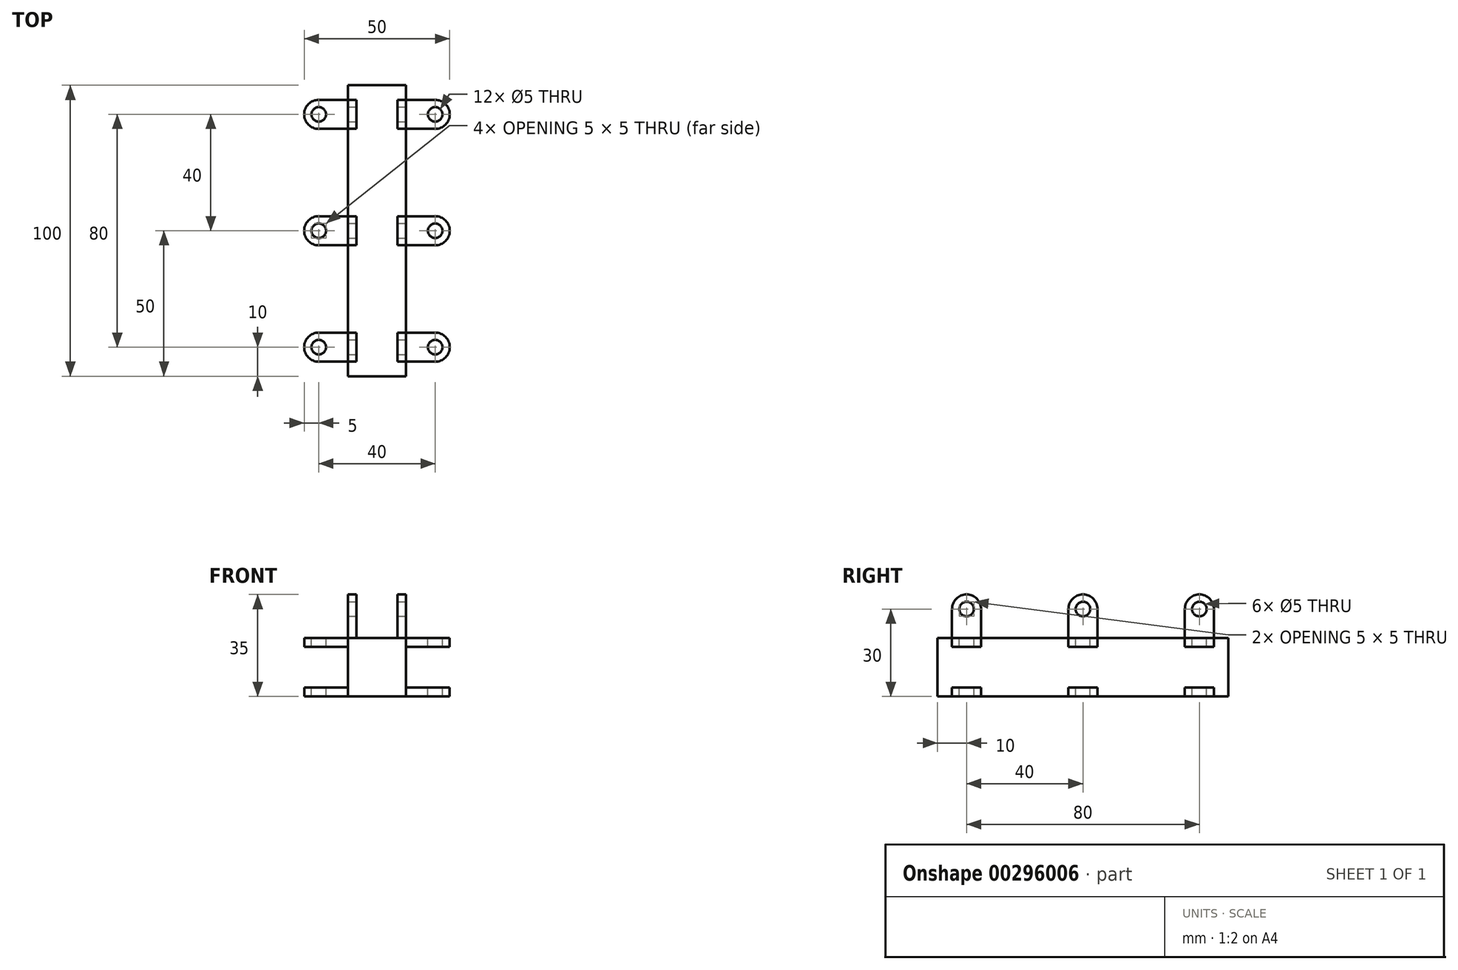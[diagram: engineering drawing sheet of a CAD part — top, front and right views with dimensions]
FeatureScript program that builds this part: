
annotation { "Feature Type Name" : "Feature", "Feature Type Description" : "" }
export const myFeature = defineFeature(function(context is Context, id is Id, definition is map)
    precondition{}
    {
        {
            var Q0;
            Q0=qCreatedBy(makeId("Front.planeOp"),FACE);
            var sketch = newSketch(context, id + "F0", { "sketchPlane" : qUnion([Q0])});
            skLineSegment(sketch, "E0.bottom", {"start": v(10, -10) * mm, "end": v(-10, -10) * mm});
            skLineSegment(sketch, "E0.top", {"start": v(10, 10) * mm, "end": v(-10, 10) * mm});
            skLineSegment(sketch, "E0.left", {"start": v(10, -10) * mm, "end": v(10, 10) * mm});
            skLineSegment(sketch, "E0.right", {"start": v(-10, -10) * mm, "end": v(-10, 10) * mm});
            skPoint(sketch, "E0.middle", {"position": v(0, 0) * mm});
            skSolve(sketch);
        }
        {
            var Q0;
            Q0=makeQuery(id+"F0.imprint","IMPRINT",FACE,{"disambiguationData":[TD([[makeQuery(id+"F0.imprint","IMPRINT",EDGE,{"derivedFrom":sQuery(id+"F0.wireOp",EDGE,"E0.bottom")}),-1.0]])]});
            extrude(context, id + "F1", {"entities" : qUnion([Q0]), "endBound" : BoundingType.SYMMETRIC, "depth" : 100 * mm});
        }
        {
            var Q0;
            Q0=qCreatedBy(makeId("Right.planeOp"),FACE);
            var sketch = newSketch(context, id + "F2", { "sketchPlane" : qUnion([Q0])});
            skLineSegment(sketch, "E1.bottom", {"start": v(-45, 10) * mm, "end": v(-35, 10) * mm});
            skLineSegment(sketch, "E1.top", {"start": v(-45, 7) * mm, "end": v(-35, 7) * mm});
            skLineSegment(sketch, "E1.left", {"start": v(-45, 10) * mm, "end": v(-45, 7) * mm});
            skLineSegment(sketch, "E1.right", {"start": v(-35, 10) * mm, "end": v(-35, 7) * mm});
            skLineSegment(sketch, "E2.MirrorCS", {"start": v(-35, -10) * mm, "end": v(-35, -7) * mm});
            skLineSegment(sketch, "E3.MirrorCS", {"start": v(-45, -10) * mm, "end": v(-45, -7) * mm});
            skLineSegment(sketch, "E4.MirrorCS", {"start": v(-45, -7) * mm, "end": v(-35, -7) * mm});
            skLineSegment(sketch, "E5.MirrorCS", {"start": v(-45, -10) * mm, "end": v(-35, -10) * mm});
            skLineSegment(sketch, "E6.MirrorCS", {"start": v(45, -10) * mm, "end": v(45, -7) * mm});
            skLineSegment(sketch, "E7.MirrorCS", {"start": v(35, -10) * mm, "end": v(35, -7) * mm});
            skLineSegment(sketch, "E8.MirrorCS", {"start": v(35, 10) * mm, "end": v(35, 7) * mm});
            skLineSegment(sketch, "E9.MirrorCS", {"start": v(45, 10) * mm, "end": v(45, 7) * mm});
            skLineSegment(sketch, "E10.MirrorCS", {"start": v(45, -7) * mm, "end": v(35, -7) * mm});
            skLineSegment(sketch, "E11.MirrorCS", {"start": v(45, 10) * mm, "end": v(35, 10) * mm});
            skLineSegment(sketch, "E12.MirrorCS", {"start": v(45, -10) * mm, "end": v(35, -10) * mm});
            skLineSegment(sketch, "E13.MirrorCS", {"start": v(45, 7) * mm, "end": v(35, 7) * mm});
            skLineSegment(sketch, "E14.bottom", {"start": v(5, 7) * mm, "end": v(-5, 7) * mm});
            skLineSegment(sketch, "E14.top", {"start": v(5, 10) * mm, "end": v(-5, 10) * mm});
            skLineSegment(sketch, "E14.left", {"start": v(5, 7) * mm, "end": v(5, 10) * mm});
            skLineSegment(sketch, "E14.right", {"start": v(-5, 7) * mm, "end": v(-5, 10) * mm});
            skPoint(sketch, "E14.middle", {"position": v(0, 8.5) * mm});
            skLineSegment(sketch, "E15.MirrorCS", {"start": v(5, -7) * mm, "end": v(5, -10) * mm});
            skLineSegment(sketch, "E16.MirrorCS", {"start": v(-5, -7) * mm, "end": v(-5, -10) * mm});
            skLineSegment(sketch, "E17.MirrorCS", {"start": v(5, -10) * mm, "end": v(-5, -10) * mm});
            skLineSegment(sketch, "E18.MirrorCS", {"start": v(5, -7) * mm, "end": v(-5, -7) * mm});
            skPoint(sketch, "E19.MirrorP", {"position": v(0, -8.5) * mm});
            skSolve(sketch);
        }
        {
            var Q0;
            Q0 = qSketchRegion(id + "F2", true);
            var Q1;
            Q1=makeQuery(id+"F1.opExtrude","SWEPT_FACE",FACE,{"disambiguationData":[OSD([sQuery(id+"F0.wireOp",EDGE,"E0.left")])]});
            extrude(context, id + "F3", {"entities" : qUnion([Q0]), "operationType" : NewBodyOperationType.ADD, "endBoundEntityFace" : qUnion([Q1]), "depth" : 25 * mm, "hasSecondDirection" : true, "secondDirectionOppositeDirection" : true, "secondDirectionDepth" : 25 * mm});
        }
        {
            var Q0;
            Q0=makeQuery(id+"F3.opExtrude","CAP_EDGE",EDGE,{"disambiguationData":[OSD([sQuery(id+"F2.wireOp",EDGE,"E1.left")])],"isStart":false});
            var Q1;
            Q1=makeQuery(id+"F3.opExtrude","CAP_EDGE",EDGE,{"disambiguationData":[OSD([sQuery(id+"F2.wireOp",EDGE,"E1.right")])],"isStart":false});
            var Q2;
            Q2=makeQuery(id+"F3.opExtrude","CAP_EDGE",EDGE,{"disambiguationData":[OSD([sQuery(id+"F2.wireOp",EDGE,"E3.MirrorCS")])],"isStart":false});
            var Q3;
            Q3=makeQuery(id+"F3.opExtrude","CAP_EDGE",EDGE,{"disambiguationData":[OSD([sQuery(id+"F2.wireOp",EDGE,"E2.MirrorCS")])],"isStart":false});
            var Q4;
            Q4=makeQuery(id+"F3.opExtrude","CAP_EDGE",EDGE,{"disambiguationData":[OSD([sQuery(id+"F2.wireOp",EDGE,"E14.right")])],"isStart":false});
            var Q5;
            Q5=makeQuery(id+"F3.opExtrude","CAP_EDGE",EDGE,{"disambiguationData":[OSD([sQuery(id+"F2.wireOp",EDGE,"E14.left")])],"isStart":false});
            var Q6;
            Q6=makeQuery(id+"F3.opExtrude","CAP_EDGE",EDGE,{"disambiguationData":[OSD([sQuery(id+"F2.wireOp",EDGE,"E16.MirrorCS")])],"isStart":false});
            var Q7;
            Q7=makeQuery(id+"F3.opExtrude","CAP_EDGE",EDGE,{"disambiguationData":[OSD([sQuery(id+"F2.wireOp",EDGE,"E15.MirrorCS")])],"isStart":false});
            var Q8;
            Q8=makeQuery(id+"F3.opExtrude","CAP_EDGE",EDGE,{"disambiguationData":[OSD([sQuery(id+"F2.wireOp",EDGE,"E8.MirrorCS")])],"isStart":false});
            var Q9;
            Q9=makeQuery(id+"F3.opExtrude","CAP_EDGE",EDGE,{"disambiguationData":[OSD([sQuery(id+"F2.wireOp",EDGE,"E9.MirrorCS")])],"isStart":false});
            var Q10;
            Q10=makeQuery(id+"F3.opExtrude","CAP_EDGE",EDGE,{"disambiguationData":[OSD([sQuery(id+"F2.wireOp",EDGE,"E7.MirrorCS")])],"isStart":false});
            var Q11;
            Q11=makeQuery(id+"F3.opExtrude","CAP_EDGE",EDGE,{"disambiguationData":[OSD([sQuery(id+"F2.wireOp",EDGE,"E6.MirrorCS")])],"isStart":false});
            fillet(context, id + "F4", {"entities" : qUnion([Q0, Q1, Q2, Q3, Q4, Q5, Q6, Q7, Q8, Q9, Q10, Q11]), "radius" : 5 * mm, "tangentPropagation" : true, "allowEdgeOverflow" : false});
        }
        {
            var Q0;
            Q0=qCreatedBy(makeId("Top.planeOp"),FACE);
            var sketch = newSketch(context, id + "F5", { "sketchPlane" : qUnion([Q0])});
            skCircle(sketch, "E20", {"center": v(20, -40) * mm, "radius": 2.5 * mm});
            skCircle(sketch, "E21.MirrorC", {"center": v(20, 40) * mm, "radius": 2.5 * mm});
            skCircle(sketch, "E22", {"center": v(20, 0) * mm, "radius": 2.5 * mm});
            skCircle(sketch, "E23.MirrorC", {"center": v(-20, -40) * mm, "radius": 2.5 * mm});
            skCircle(sketch, "E24.MirrorC", {"center": v(-20, 0) * mm, "radius": 2.5 * mm});
            skCircle(sketch, "E25.MirrorC", {"center": v(-20, 40) * mm, "radius": 2.5 * mm});
            skSolve(sketch);
        }
        {
            var Q0;
            Q0 = qSketchRegion(id + "F5", true);
            extrude(context, id + "F6", {"entities" : qUnion([Q0]), "operationType" : NewBodyOperationType.REMOVE, "endBound" : BoundingType.SYMMETRIC, "oppositeDirection" : true, "depth" : 20 * mm});
        }
        {
            var Q0;
            Q0=makeQuery(id+"F3.opExtrude","CAP_EDGE",EDGE,{"disambiguationData":[OSD([sQuery(id+"F2.wireOp",EDGE,"E3.MirrorCS")])],"isStart":true});
            var Q1;
            Q1=makeQuery(id+"F3.opExtrude","CAP_EDGE",EDGE,{"disambiguationData":[OSD([sQuery(id+"F2.wireOp",EDGE,"E2.MirrorCS")])],"isStart":true});
            var Q2;
            Q2=makeQuery(id+"F3.opExtrude","CAP_EDGE",EDGE,{"disambiguationData":[OSD([sQuery(id+"F2.wireOp",EDGE,"E1.left")])],"isStart":true});
            var Q3;
            Q3=makeQuery(id+"F3.opExtrude","CAP_EDGE",EDGE,{"disambiguationData":[OSD([sQuery(id+"F2.wireOp",EDGE,"E1.right")])],"isStart":true});
            var Q4;
            Q4=makeQuery(id+"F3.opExtrude","CAP_EDGE",EDGE,{"disambiguationData":[OSD([sQuery(id+"F2.wireOp",EDGE,"E16.MirrorCS")])],"isStart":true});
            var Q5;
            Q5=makeQuery(id+"F3.opExtrude","CAP_EDGE",EDGE,{"disambiguationData":[OSD([sQuery(id+"F2.wireOp",EDGE,"E15.MirrorCS")])],"isStart":true});
            var Q6;
            Q6=makeQuery(id+"F3.opExtrude","CAP_EDGE",EDGE,{"disambiguationData":[OSD([sQuery(id+"F2.wireOp",EDGE,"E14.right")])],"isStart":true});
            var Q7;
            Q7=makeQuery(id+"F3.opExtrude","CAP_EDGE",EDGE,{"disambiguationData":[OSD([sQuery(id+"F2.wireOp",EDGE,"E14.left")])],"isStart":true});
            var Q8;
            Q8=makeQuery(id+"F3.opExtrude","CAP_EDGE",EDGE,{"disambiguationData":[OSD([sQuery(id+"F2.wireOp",EDGE,"E7.MirrorCS")])],"isStart":true});
            var Q9;
            Q9=makeQuery(id+"F3.opExtrude","CAP_EDGE",EDGE,{"disambiguationData":[OSD([sQuery(id+"F2.wireOp",EDGE,"E6.MirrorCS")])],"isStart":true});
            var Q10;
            Q10=makeQuery(id+"F3.opExtrude","CAP_EDGE",EDGE,{"disambiguationData":[OSD([sQuery(id+"F2.wireOp",EDGE,"E8.MirrorCS")])],"isStart":true});
            var Q11;
            Q11=makeQuery(id+"F3.opExtrude","CAP_EDGE",EDGE,{"disambiguationData":[OSD([sQuery(id+"F2.wireOp",EDGE,"E9.MirrorCS")])],"isStart":true});
            fillet(context, id + "F7", {"entities" : qUnion([Q0, Q1, Q2, Q3, Q4, Q5, Q6, Q7, Q8, Q9, Q10, Q11]), "radius" : 5 * mm, "tangentPropagation" : true, "allowEdgeOverflow" : false});
        }
        {
            var Q0;
            Q0=qCreatedBy(makeId("Top.planeOp"),FACE);
            var sketch = newSketch(context, id + "F8", { "sketchPlane" : qUnion([Q0])});
            skLineSegment(sketch, "E26.bottom", {"start": v(10, -5) * mm, "end": v(7, -5) * mm});
            skLineSegment(sketch, "E26.top", {"start": v(10, 5) * mm, "end": v(7, 5) * mm});
            skLineSegment(sketch, "E26.left", {"start": v(10, -5) * mm, "end": v(10, 5) * mm});
            skLineSegment(sketch, "E26.right", {"start": v(7, -5) * mm, "end": v(7, 5) * mm});
            skLineSegment(sketch, "E27.MirrorCS", {"start": v(-7, -5) * mm, "end": v(-7, 5) * mm});
            skLineSegment(sketch, "E28.MirrorCS", {"start": v(-10, -5) * mm, "end": v(-10, 5) * mm});
            skLineSegment(sketch, "E29.MirrorCS", {"start": v(-10, 5) * mm, "end": v(-7, 5) * mm});
            skLineSegment(sketch, "E30.MirrorCS", {"start": v(-10, -5) * mm, "end": v(-7, -5) * mm});
            skLineSegment(sketch, "E31.bottom", {"start": v(10, 45) * mm, "end": v(7, 45) * mm});
            skLineSegment(sketch, "E31.top", {"start": v(10, 35) * mm, "end": v(7, 35) * mm});
            skLineSegment(sketch, "E31.left", {"start": v(10, 45) * mm, "end": v(10, 35) * mm});
            skLineSegment(sketch, "E31.right", {"start": v(7, 45) * mm, "end": v(7, 35) * mm});
            skLineSegment(sketch, "E32.MirrorCS", {"start": v(-7, 45) * mm, "end": v(-7, 35) * mm});
            skLineSegment(sketch, "E33.MirrorCS", {"start": v(-10, 45) * mm, "end": v(-10, 35) * mm});
            skLineSegment(sketch, "E34.MirrorCS", {"start": v(-10, 35) * mm, "end": v(-7, 35) * mm});
            skLineSegment(sketch, "E35.MirrorCS", {"start": v(-10, 45) * mm, "end": v(-7, 45) * mm});
            skLineSegment(sketch, "E36.MirrorCS", {"start": v(-7, -45) * mm, "end": v(-7, -35) * mm});
            skLineSegment(sketch, "E37.MirrorCS", {"start": v(7, -45) * mm, "end": v(7, -35) * mm});
            skLineSegment(sketch, "E38.MirrorCS", {"start": v(-10, -35) * mm, "end": v(-7, -35) * mm});
            skLineSegment(sketch, "E39.MirrorCS", {"start": v(-10, -45) * mm, "end": v(-7, -45) * mm});
            skLineSegment(sketch, "E40.MirrorCS", {"start": v(10, -45) * mm, "end": v(7, -45) * mm});
            skLineSegment(sketch, "E41.MirrorCS", {"start": v(10, -35) * mm, "end": v(7, -35) * mm});
            skLineSegment(sketch, "E42.MirrorCS", {"start": v(-10, -45) * mm, "end": v(-10, -35) * mm});
            skLineSegment(sketch, "E43.MirrorCS", {"start": v(10, -45) * mm, "end": v(10, -35) * mm});
            skSolve(sketch);
        }
        {
            var Q0;
            Q0 = qSketchRegion(id + "F8", true);
            extrude(context, id + "F9", {"entities" : qUnion([Q0]), "operationType" : NewBodyOperationType.ADD, "depth" : 25 * mm});
        }
        {
            var Q0;
            Q0=makeQuery(id+"F9.opExtrude","CAP_EDGE",EDGE,{"disambiguationData":[OSD([sQuery(id+"F8.wireOp",EDGE,"e20e8f79-4628-48e8-b713-7d486e24c0815.MirrorCS")])],"isStart":false});
            var Q1;
            Q1=makeQuery(id+"F9.opExtrude","CAP_EDGE",EDGE,{"disambiguationData":[OSD([sQuery(id+"F8.wireOp",EDGE,"e20e8f79-4628-48e8-b713-7d486e24c0817.MirrorCS")])],"isStart":false});
            var Q2;
            Q2=makeQuery(id+"F9.opExtrude","CAP_EDGE",EDGE,{"disambiguationData":[OSD([sQuery(id+"F8.wireOp",EDGE,"e20e8f79-4628-48e8-b713-7d486e24c0811.MirrorCS")])],"isStart":false});
            var Q3;
            Q3=makeQuery(id+"F9.opExtrude","CAP_EDGE",EDGE,{"disambiguationData":[OSD([sQuery(id+"F8.wireOp",EDGE,"e20e8f79-4628-48e8-b713-7d486e24c0812.MirrorCS")])],"isStart":false});
            var Q4;
            Q4=makeQuery(id+"F9.opExtrude","CAP_EDGE",EDGE,{"disambiguationData":[OSD([sQuery(id+"F8.wireOp",EDGE,"E26.bottom")])],"isStart":false});
            var Q5;
            Q5=makeQuery(id+"F9.opExtrude","CAP_EDGE",EDGE,{"disambiguationData":[OSD([sQuery(id+"F8.wireOp",EDGE,"E26.top")])],"isStart":false});
            var Q6;
            Q6=makeQuery(id+"F9.opExtrude","CAP_EDGE",EDGE,{"disambiguationData":[OSD([sQuery(id+"F8.wireOp",EDGE,"E30.MirrorCS")])],"isStart":false});
            var Q7;
            Q7=makeQuery(id+"F9.opExtrude","CAP_EDGE",EDGE,{"disambiguationData":[OSD([sQuery(id+"F8.wireOp",EDGE,"E29.MirrorCS")])],"isStart":false});
            var Q8;
            Q8=makeQuery(id+"F9.opExtrude","CAP_EDGE",EDGE,{"disambiguationData":[OSD([sQuery(id+"F8.wireOp",EDGE,"037edfc9-c22c-4f75-90ba-cc2340fa92b612.MirrorCS")])],"isStart":false});
            var Q9;
            Q9=makeQuery(id+"F9.opExtrude","CAP_EDGE",EDGE,{"disambiguationData":[OSD([sQuery(id+"F8.wireOp",EDGE,"037edfc9-c22c-4f75-90ba-cc2340fa92b611.MirrorCS")])],"isStart":false});
            var Q10;
            Q10=makeQuery(id+"F9.opExtrude","CAP_EDGE",EDGE,{"disambiguationData":[OSD([sQuery(id+"F8.wireOp",EDGE,"037edfc9-c22c-4f75-90ba-cc2340fa92b618.MirrorCS")])],"isStart":false});
            var Q11;
            Q11=makeQuery(id+"F9.opExtrude","CAP_EDGE",EDGE,{"disambiguationData":[OSD([sQuery(id+"F8.wireOp",EDGE,"037edfc9-c22c-4f75-90ba-cc2340fa92b619.MirrorCS")])],"isStart":false});
            fillet(context, id + "F10", {"entities" : qUnion([Q0, Q1, Q2, Q3, Q4, Q5, Q6, Q7, Q8, Q9, Q10, Q11]), "radius" : 5 * mm, "tangentPropagation" : true, "allowEdgeOverflow" : false});
        }
        {
            var Q0;
            Q0=qCreatedBy(makeId("Right.planeOp"),FACE);
            var sketch = newSketch(context, id + "F11", { "sketchPlane" : qUnion([Q0])});
            skCircle(sketch, "E44", {"center": v(-40, 20) * mm, "radius": 2.5 * mm});
            skCircle(sketch, "E45.MirrorC", {"center": v(40, 20) * mm, "radius": 2.5 * mm});
            skCircle(sketch, "E46", {"center": v(0, 20) * mm, "radius": 2.5 * mm});
            skSolve(sketch);
        }
        {
            var Q0;
            Q0 = qSketchRegion(id + "F8", true);
            extrude(context, id + "F12", {"entities" : qUnion([Q0]), "operationType" : NewBodyOperationType.ADD, "depth" : 25 * mm});
        }
        {
            var Q0;
            Q0=makeQuery(id+"F9.opExtrude","CAP_EDGE",EDGE,{"disambiguationData":[OSD([sQuery(id+"F8.wireOp",EDGE,"E31.bottom")])],"isStart":false});
            var Q1;
            Q1=makeQuery(id+"F9.opExtrude","CAP_EDGE",EDGE,{"disambiguationData":[OSD([sQuery(id+"F8.wireOp",EDGE,"E35.MirrorCS")])],"isStart":false});
            var Q2;
            Q2=makeQuery(id+"F9.opExtrude","CAP_EDGE",EDGE,{"disambiguationData":[OSD([sQuery(id+"F8.wireOp",EDGE,"E34.MirrorCS")])],"isStart":false});
            var Q3;
            Q3=makeQuery(id+"F9.opExtrude","CAP_EDGE",EDGE,{"disambiguationData":[OSD([sQuery(id+"F8.wireOp",EDGE,"E31.top")])],"isStart":false});
            var Q4;
            Q4=makeQuery(id+"F12.opExtrude","CAP_EDGE",EDGE,{"disambiguationData":[OSD([sQuery(id+"F8.wireOp",EDGE,"E26.top")])],"isStart":false});
            var Q5;
            Q5=makeQuery(id+"F12.opExtrude","CAP_EDGE",EDGE,{"disambiguationData":[OSD([sQuery(id+"F8.wireOp",EDGE,"E26.bottom")])],"isStart":false});
            var Q6;
            Q6=makeQuery(id+"F12.opExtrude","CAP_EDGE",EDGE,{"disambiguationData":[OSD([sQuery(id+"F8.wireOp",EDGE,"E29.MirrorCS")])],"isStart":false});
            var Q7;
            Q7=makeQuery(id+"F12.opExtrude","CAP_EDGE",EDGE,{"disambiguationData":[OSD([sQuery(id+"F8.wireOp",EDGE,"E30.MirrorCS")])],"isStart":false});
            var Q8;
            Q8=makeQuery(id+"F9.opExtrude","CAP_EDGE",EDGE,{"disambiguationData":[OSD([sQuery(id+"F8.wireOp",EDGE,"E41.MirrorCS")])],"isStart":false});
            var Q9;
            Q9=makeQuery(id+"F9.opExtrude","CAP_EDGE",EDGE,{"disambiguationData":[OSD([sQuery(id+"F8.wireOp",EDGE,"E40.MirrorCS")])],"isStart":false});
            var Q10;
            Q10=makeQuery(id+"F9.opExtrude","CAP_EDGE",EDGE,{"disambiguationData":[OSD([sQuery(id+"F8.wireOp",EDGE,"E38.MirrorCS")])],"isStart":false});
            var Q11;
            Q11=makeQuery(id+"F9.opExtrude","CAP_EDGE",EDGE,{"disambiguationData":[OSD([sQuery(id+"F8.wireOp",EDGE,"E39.MirrorCS")])],"isStart":false});
            fillet(context, id + "F13", {"entities" : qUnion([Q0, Q1, Q2, Q3, Q4, Q5, Q6, Q7, Q8, Q9, Q10, Q11]), "radius" : 5 * mm, "tangentPropagation" : true, "allowEdgeOverflow" : false});
        }
        {
            var Q0;
            Q0 = qSketchRegion(id + "F11", true);
            extrude(context, id + "F14", {"entities" : qUnion([Q0]), "operationType" : NewBodyOperationType.REMOVE, "endBound" : BoundingType.SYMMETRIC, "oppositeDirection" : true, "depth" : 20 * mm});
        }
    });
